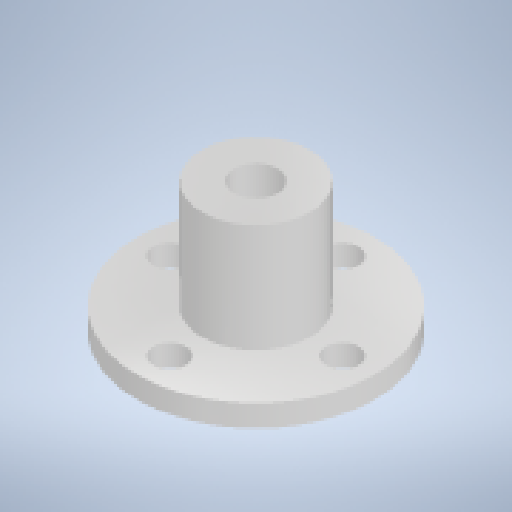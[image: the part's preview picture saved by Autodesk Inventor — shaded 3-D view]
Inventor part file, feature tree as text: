
AUTODESK INVENTOR PART (.ipt)
format: ipt  version: 2023.1 (Build 271208000, 208)  size: 256,000 bytes
history: native  units: mm
features: sketch x3, extrude x2, hole x1
ambient origin geometry x8: Origin, YZ Plane, XZ Plane, XY Plane, X Axis, Y Axis, Z Axis, Center Point
bodies: Solid1 (feature_tree)
feature tree (6):
  extrude  "Extrusion1"  Depth=2.0mm TaperAngle=0.0deg
  extrude  "Extrusion2"  Depth=10.0mm TaperAngle=0.0deg
  hole  "Hole1"  [1 undecoded]
  sketch  "Sketch1"  dims[d0=22.0mm d1=2.0mm d2=0.0mm]
  sketch  "Sketch2"  dims[d3=10.0mm d4=10.0mm d5=0.0mm]
  sketch  "Sketch3"  dims[d6=4.0mm d7=4.0mm d8=6.0mm d9=4.0mm d10=2.0mm d11=90.0deg d12=8.0mm d13=20.594885mm d15=3.0mm d16=40.0mm d18=360.0deg]
note: 1 required parameter value undecoded (feature->parameter linkage not recoverable at this tier; creation-order binding heuristic only, values carry confidence <= 0.55)
